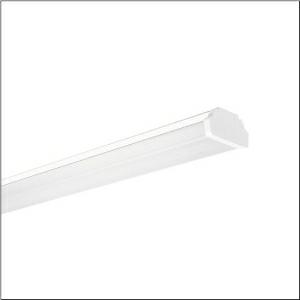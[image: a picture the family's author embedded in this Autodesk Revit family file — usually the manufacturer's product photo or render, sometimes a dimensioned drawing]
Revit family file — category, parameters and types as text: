
# Revit family: dus_r__31_mo_53bd812c1v4075_b8a3
name_source: partatom
category: Lighting Fixtures
units: mm (PartAtom-declared; Revit-internal decimal feet)

## family parameters
Cut with Voids When Loaded = No
Host = Face
Light Source = No
Part Type = Normal
Room Calculation Point = No
Round Connector Dimension = Use Diameter
Shared = No

## types (1)
- --- (1 x LED, 7620 lm, 48.9 W, 4000K)
    Apparent Load = 49 VA
    CIE Flux Codes = 47 80 95 92 100
    Color Rendering = 80
    Color Temperature = 4000K
    Default Elevation = 1800 mm
    Description = DUS® 31 MOluminaire insert, length: 1.535mm, width: 81mm, height: 90mm, LED rated luminous flux: 7.620lm, light colour: 840, control gear: ON/OFF Multilumen, CLOi, control gear: ECG Multilumen, with plug, 3-pole, with phase selection, mains connection: 220..240V, AC, 50/60Hz, primary optical cover: cover, of PMMA, light emission: direct distribution, primary light characteristic: symmetric, protection rating (complete): IP20, protection rating (LED compartment): IP50, insulation class (complete): insulation class I (protective earthing), certification: CE, ENEC, VDE, UKCA, permissible ambient temperature for indoor applications: -35..+30°C, corresponds to IFS (International Featured Standards) requirements for safety and quality in the food industry, reducing of maximum allowable ambient temperature of 5°C with ceiling mounting, packaging unit: 1 piece
    Height = 95 mm
    Lamp = 1 x LED
    Lamp Light Flux = 7620 lm
    Lamp Power = 48.9 W
    Lamp count = 1
    Length = 1535 mm
    Luminous efficacy = 156 lm/W
    Manufacturer = Siteco
    ModVariant = No
    Model = 53BD812C1V4075
    Mounting Place = Ceiling
    Mounting Type = Pendant
    Number of Poles = 1
    OnlyDefault = Yes
    Power Factor = 1
    Product Name = DUS® 31 MO
    Product group = luminaire insert
    ProductGroupID = 902
    Protection Class = Protection class I
    Protection Degree = IP 20
    RLX_Detail_Level = 1
    RlxData = <blob elided: 39605 chars, md5=ee409082>
    Socket = socket
    Standby Power = 0 W
    System Light Flux = 7620 lm
    System Power = 49 W
    Type Comments = factory setting: luminous flux: 100 % | (A | C | E) | 107 mA
    Type Image = l_1003451.jpg
    URL = http://relux.com
    VarID = @adj_131333
    Voltage = 0 V
    Weight = 0.00 kg
    Width = 81 mm

## geometry (parser evidence)
native form markers: Blend x4, Sweep x11
no freeform markers — native parametric forms only
